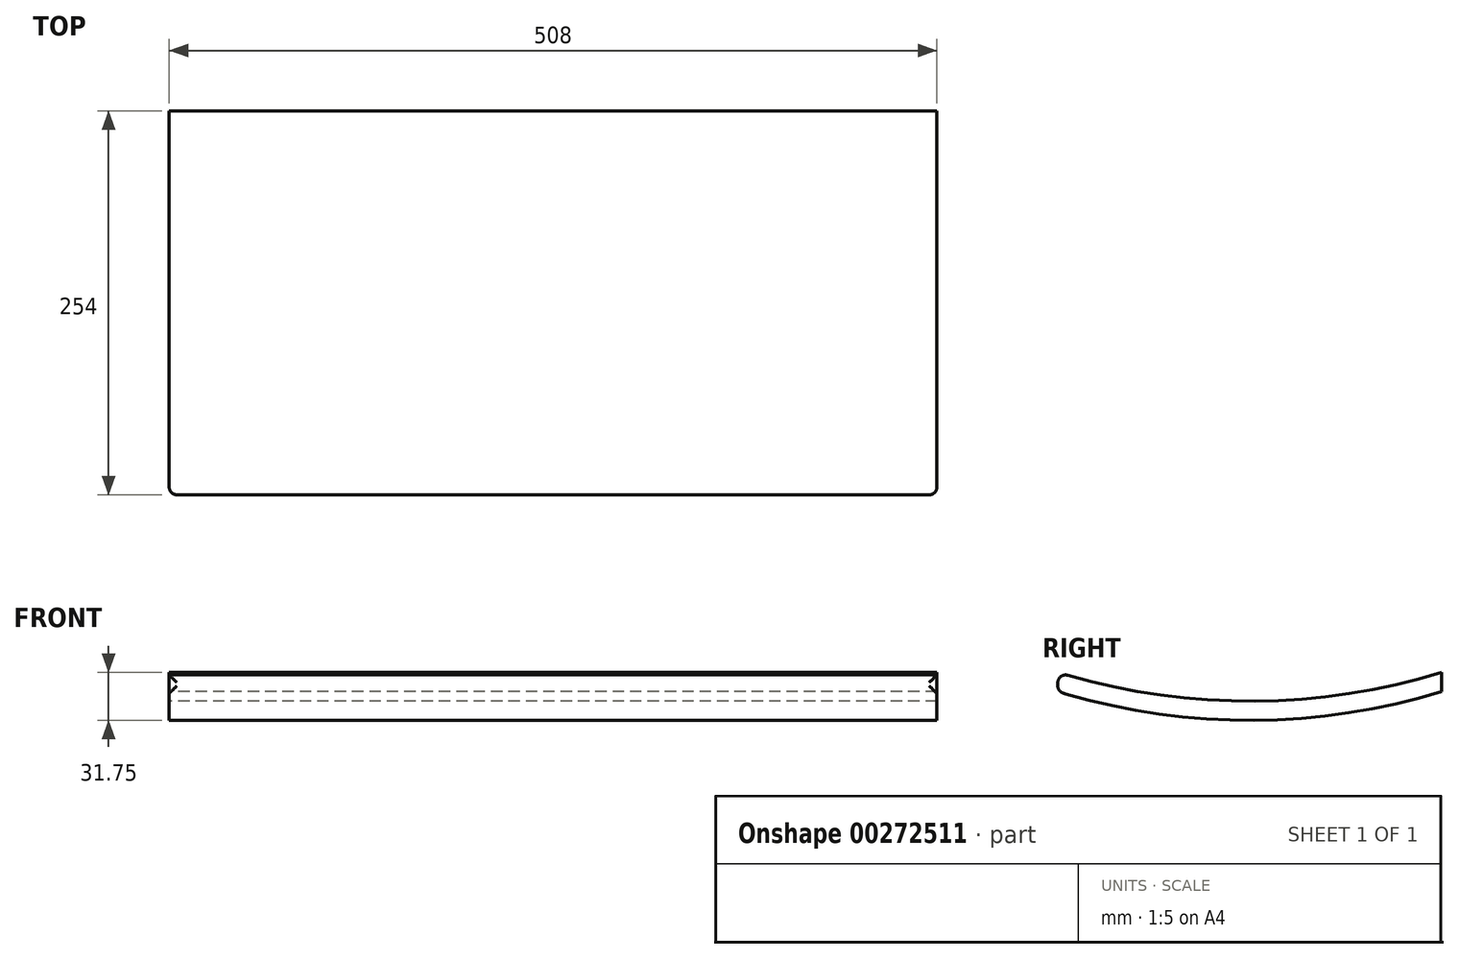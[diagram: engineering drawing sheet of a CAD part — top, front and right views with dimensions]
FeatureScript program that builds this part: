
annotation { "Feature Type Name" : "Feature", "Feature Type Description" : "" }
export const myFeature = defineFeature(function(context is Context, id is Id, definition is map)
    precondition{}
    {
        {
            var Q0;
            Q0=qCreatedBy(makeId("Right.planeOp"),FACE);
            var sketch = newSketch(context, id + "F0", { "sketchPlane" : qUnion([Q0])});
            skPoint(sketch, "E0.middle", {"position": v(0, 0) * mm});
            skPoint(sketch, "E1", {"position": v(-109.54, -26.83) * mm});
            skPoint(sketch, "E2.orphan", {"position": v(-346.07, -34.6) * mm});
            skPoint(sketch, "E3.orphan", {"position": v(127, -19.05) * mm});
            skPoint(sketch, "E0.left.end.orphan", {"position": v(236.54, 7.78) * mm});
            skPoint(sketch, "E4.end.orphan", {"position": v(-236.54, -7.78) * mm});
            skLineSegment(sketch, "E5.left", {"start": v(127, -19.05) * mm, "end": v(127, -19.05) * mm});
            skLineSegment(sketch, "E6.left", {"start": v(127, 6.35) * mm, "end": v(127, 19.05) * mm});
            skPoint(sketch, "E7.orphan", {"position": v(346.07, 34.6) * mm});
            skArc(sketch, "E8", {"start": v(-127, 19.05) * mm, "mid": v(0, 0) * mm, "end": v(127, 19.05) * mm});
            skLineSegment(sketch, "E9", {"start": v(127, 19.05) * mm, "end": v(127, 6.35) * mm});
            skLineSegment(sketch, "E10", {"start": v(-127, 19.05) * mm, "end": v(-127, 6.35) * mm});
            skArc(sketch, "E11", {"start": v(-127, 6.35) * mm, "mid": v(0, -12.7) * mm, "end": v(127, 6.35) * mm});
            skPoint(sketch, "E12.end.orphan", {"position": v(0, -12.7) * mm});
            skSolve(sketch);
        }
        {
            var Q0;
            Q0 = qSketchRegion(id + "F0", true);
            extrude(context, id + "F1", {"entities" : qUnion([Q0]), "depth" : 254 * mm, "offsetDistance" : 25.4 * mm, "hasSecondDirection" : true, "secondDirectionOppositeDirection" : true, "secondDirectionDepth" : 254 * mm});
        }
        {
            var Q0;
            Q0=makeQuery(id+"F1.opExtrude","SWEPT_FACE",FACE,{"disambiguationData":[OSD([sQuery(id+"F0.wireOp",EDGE,"E9")])]});
            var Q1;
            Q1=makeQuery(id+"F1.opExtrude","SWEPT_FACE",FACE,{"disambiguationData":[OSD([sQuery(id+"F0.wireOp",EDGE,"E10")])]});
            fillet(context, id + "F2", {"entities" : qUnion([Q0, Q1]), "radius" : 5.08 * mm, "tangentPropagation" : true, "allowEdgeOverflow" : false});
        }
    });
